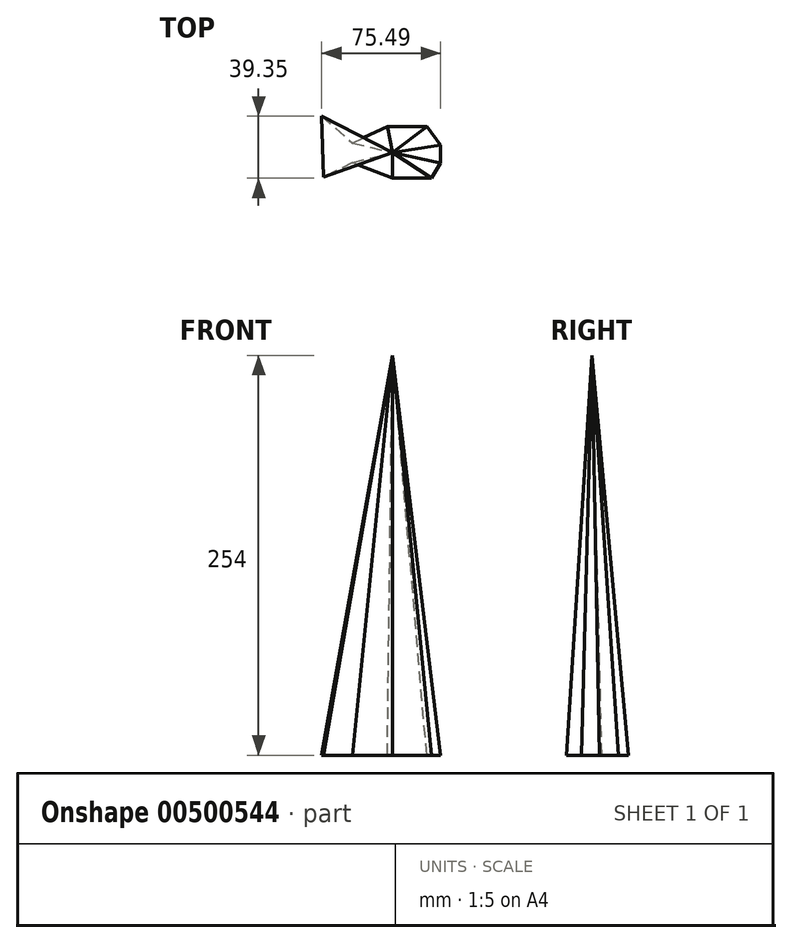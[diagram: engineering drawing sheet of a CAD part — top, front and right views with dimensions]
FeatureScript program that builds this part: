
annotation { "Feature Type Name" : "Feature", "Feature Type Description" : "" }
export const myFeature = defineFeature(function(context is Context, id is Id, definition is map)
    precondition{}
    {
        {
            var Q0;
            Q0=qCreatedBy(makeId("Top.planeOp"),FACE);
            var sketch = newSketch(context, id + "F0", { "sketchPlane" : qUnion([Q0])});
            skLineSegment(sketch, "E0", {"start": v(-44.89, 23.17) * mm, "end": v(-25.36, 6.27) * mm});
            skLineSegment(sketch, "E1", {"start": v(-25.36, 6.27) * mm, "end": v(-3.2, 16.76) * mm});
            skLineSegment(sketch, "E2", {"start": v(-3.2, 16.76) * mm, "end": v(21.86, 16.76) * mm});
            skLineSegment(sketch, "E3", {"start": v(21.86, 16.76) * mm, "end": v(30.6, 4.8) * mm});
            skLineSegment(sketch, "E4", {"start": v(30.6, 4.8) * mm, "end": v(30.6, -6.56) * mm});
            skLineSegment(sketch, "E5", {"start": v(30.6, -6.56) * mm, "end": v(24.78, -16.18) * mm});
            skLineSegment(sketch, "E6", {"start": v(24.78, -16.18) * mm, "end": v(0, -16.18) * mm});
            skLineSegment(sketch, "E7", {"start": v(0, -16.18) * mm, "end": v(-25.36, -6.27) * mm});
            skLineSegment(sketch, "E8", {"start": v(-25.36, -6.27) * mm, "end": v(-43.72, -15.6) * mm});
            skLineSegment(sketch, "E9", {"start": v(-43.72, -15.6) * mm, "end": v(-44.89, 23.17) * mm});
            skSolve(sketch);
        }
        {
            var Q0;
            Q0=qCreatedBy(makeId("Top.planeOp"),FACE);
            cPlane(context, id + "F1", {"entities" : qUnion([Q0]), "cplaneType" : CPlaneType.OFFSET, "offset" : 254 * mm, "width" : 152.4 * mm, "height" : 152.4 * mm});
        }
        {
            var Q0;
            Q0=qCreatedBy(id+"F1.planeOp",FACE);
            var sketch = newSketch(context, id + "F2", { "sketchPlane" : qUnion([Q0])});
            skPoint(sketch, "E10", {"position": v(0, 0) * mm});
            skSolve(sketch);
        }
        {
            var Q0;
            Q0=makeQuery(id+"F0.imprint","IMPRINT",FACE,{"disambiguationData":[TD([[makeQuery(id+"F0.imprint","IMPRINT",EDGE,{"derivedFrom":sQuery(id+"F0.wireOp",EDGE,"E0")}),-1.0]])]});
            var Q1;
            Q1=sQuery(id+"F2.wireOp",VERTEX,"E10");
            loft(context, id + "F3", {"sheetProfilesArray" : [{ "sheetProfileEntities" : qUnion([Q0]) }, { "sheetProfileEntities" : qUnion([Q1]) }]});
        }
    });
